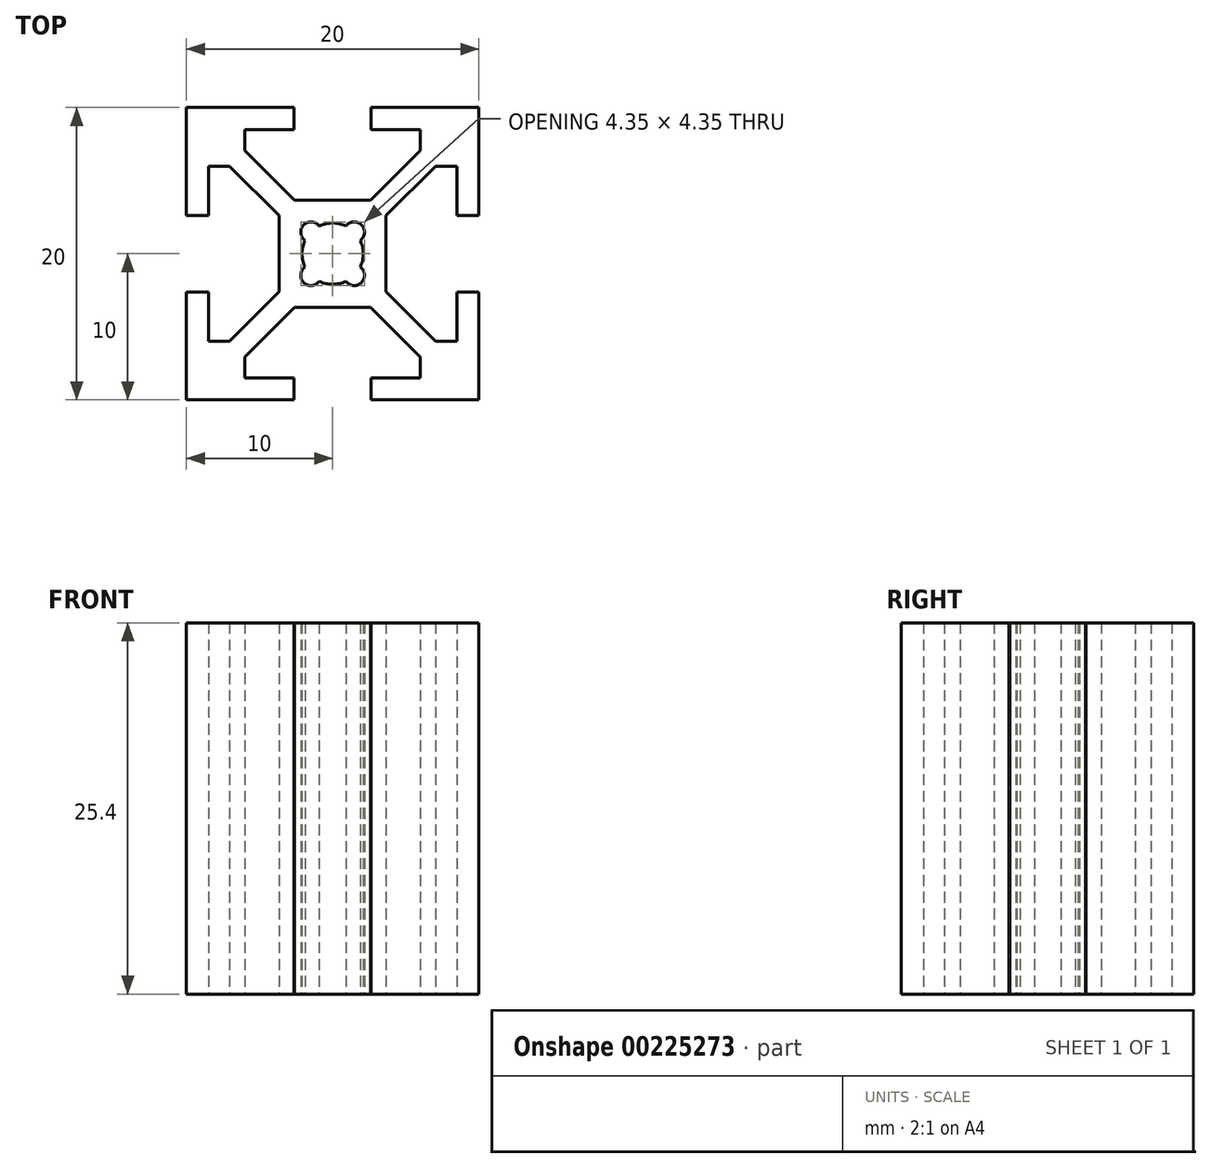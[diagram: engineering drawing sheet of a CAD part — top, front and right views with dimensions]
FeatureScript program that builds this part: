
annotation { "Feature Type Name" : "Feature", "Feature Type Description" : "" }
export const myFeature = defineFeature(function(context is Context, id is Id, definition is map)
    precondition{}
    {
        {
            var Q0;
            Q0=qCreatedBy(makeId("Top.planeOp"),FACE);
            var sketch = newSketch(context, id + "F0", { "sketchPlane" : qUnion([Q0])});
            skLineSegment(sketch, "E0.bottom", {"start": v(10, 10) * mm, "end": v(-10, 10) * mm});
            skLineSegment(sketch, "E0.top", {"start": v(10, -10) * mm, "end": v(-10, -10) * mm});
            skLineSegment(sketch, "E0.left", {"start": v(10, 10) * mm, "end": v(10, -10) * mm});
            skLineSegment(sketch, "E0.right", {"start": v(-10, 10) * mm, "end": v(-10, -10) * mm});
            skPoint(sketch, "E0.middle", {"position": v(0, 0) * mm});
            skLineSegment(sketch, "E1", {"start": v(-10, 10) * mm, "end": v(10, -10) * mm, "construction": true});
            skLineSegment(sketch, "E2", {"start": v(-10, -10) * mm, "end": v(10, 10) * mm, "construction": true});
            skLineSegment(sketch, "E3", {"start": v(0, 10) * mm, "end": v(0, -10) * mm, "construction": true});
            skLineSegment(sketch, "E4", {"start": v(-10, 0) * mm, "end": v(10, 0) * mm, "construction": true});
            skPoint(sketch, "E4.endSnap0", {"position": v(10, 0) * mm});
            skLineSegment(sketch, "E5", {"start": v(-2.63, 13.49) * mm, "end": v(2.63, 13.49) * mm});
            skLineSegment(sketch, "E6", {"start": v(2.63, 13.49) * mm, "end": v(2.63, 8.5) * mm});
            skLineSegment(sketch, "E7", {"start": v(2.63, 8.5) * mm, "end": v(6, 8.5) * mm});
            skLineSegment(sketch, "E8", {"start": v(6, 8.5) * mm, "end": v(6, 7.06) * mm});
            skLineSegment(sketch, "E9", {"start": v(6, 7.06) * mm, "end": v(2.6, 3.66) * mm});
            skLineSegment(sketch, "E10", {"start": v(2.6, 3.66) * mm, "end": v(-2.6, 3.66) * mm});
            skLineSegment(sketch, "E11", {"start": v(-2.6, 3.66) * mm, "end": v(-6, 7.06) * mm});
            skLineSegment(sketch, "E12", {"start": v(-6, 7.06) * mm, "end": v(-6, 8.5) * mm});
            skLineSegment(sketch, "E13", {"start": v(-6, 8.5) * mm, "end": v(-2.63, 8.5) * mm});
            skLineSegment(sketch, "E14", {"start": v(-2.63, 8.5) * mm, "end": v(-2.63, 13.49) * mm});
            skCircle(sketch, "E15", {"center": v(0, 0) * mm, "radius": 2.1 * mm});
            skLineSegment(sketch, "E16.MirrorCS", {"start": v(-7.06, 6) * mm, "end": v(-8.5, 6) * mm});
            skLineSegment(sketch, "E17.MirrorCS", {"start": v(-3.66, 2.6) * mm, "end": v(-7.06, 6) * mm});
            skLineSegment(sketch, "E18.MirrorCS", {"start": v(-8.5, 6) * mm, "end": v(-8.5, 2.63) * mm});
            skLineSegment(sketch, "E19.MirrorCS", {"start": v(-3.66, -2.6) * mm, "end": v(-3.66, 2.6) * mm});
            skLineSegment(sketch, "E20.MirrorCS", {"start": v(-7.06, -6) * mm, "end": v(-3.66, -2.6) * mm});
            skLineSegment(sketch, "E21.MirrorCS", {"start": v(-8.5, -6) * mm, "end": v(-7.06, -6) * mm});
            skLineSegment(sketch, "E22.MirrorCS", {"start": v(-8.5, -2.63) * mm, "end": v(-8.5, -6) * mm});
            skLineSegment(sketch, "E23.MirrorCS", {"start": v(-13.49, -2.63) * mm, "end": v(-8.5, -2.63) * mm});
            skLineSegment(sketch, "E24.MirrorCS", {"start": v(-13.49, 2.63) * mm, "end": v(-13.49, -2.63) * mm});
            skLineSegment(sketch, "E25.MirrorCS", {"start": v(-8.5, 2.63) * mm, "end": v(-13.49, 2.63) * mm});
            skLineSegment(sketch, "E26.MirrorCS", {"start": v(-2.6, -3.66) * mm, "end": v(-6, -7.06) * mm});
            skLineSegment(sketch, "E27.MirrorCS", {"start": v(2.6, -3.66) * mm, "end": v(-2.6, -3.66) * mm});
            skLineSegment(sketch, "E28.MirrorCS", {"start": v(6, -7.06) * mm, "end": v(2.6, -3.66) * mm});
            skLineSegment(sketch, "E29.MirrorCS", {"start": v(6, -8.5) * mm, "end": v(6, -7.06) * mm});
            skLineSegment(sketch, "E30.MirrorCS", {"start": v(2.63, -8.5) * mm, "end": v(6, -8.5) * mm});
            skLineSegment(sketch, "E31.MirrorCS", {"start": v(2.63, -13.49) * mm, "end": v(2.63, -8.5) * mm});
            skLineSegment(sketch, "E32.MirrorCS", {"start": v(-2.63, -13.49) * mm, "end": v(2.63, -13.49) * mm});
            skLineSegment(sketch, "E33.MirrorCS", {"start": v(-2.63, -8.5) * mm, "end": v(-2.63, -13.49) * mm});
            skLineSegment(sketch, "E34.MirrorCS", {"start": v(-6, -8.5) * mm, "end": v(-2.63, -8.5) * mm});
            skLineSegment(sketch, "E35.MirrorCS", {"start": v(-6, -7.06) * mm, "end": v(-6, -8.5) * mm});
            skLineSegment(sketch, "E36.MirrorCS", {"start": v(7.06, 6) * mm, "end": v(3.66, 2.6) * mm});
            skLineSegment(sketch, "E37.MirrorCS", {"start": v(8.5, 6) * mm, "end": v(7.06, 6) * mm});
            skLineSegment(sketch, "E38.MirrorCS", {"start": v(8.5, 2.63) * mm, "end": v(8.5, 6) * mm});
            skLineSegment(sketch, "E39.MirrorCS", {"start": v(13.49, 2.63) * mm, "end": v(8.5, 2.63) * mm});
            skLineSegment(sketch, "E40.MirrorCS", {"start": v(13.49, -2.63) * mm, "end": v(13.49, 2.63) * mm});
            skLineSegment(sketch, "E41.MirrorCS", {"start": v(8.5, -2.63) * mm, "end": v(13.49, -2.63) * mm});
            skLineSegment(sketch, "E42.MirrorCS", {"start": v(8.5, -6) * mm, "end": v(8.5, -2.63) * mm});
            skLineSegment(sketch, "E43.MirrorCS", {"start": v(7.06, -6) * mm, "end": v(8.5, -6) * mm});
            skLineSegment(sketch, "E44.MirrorCS", {"start": v(3.66, -2.6) * mm, "end": v(7.06, -6) * mm});
            skLineSegment(sketch, "E45.MirrorCS", {"start": v(3.66, 2.6) * mm, "end": v(3.66, -2.6) * mm});
            skCircle(sketch, "E46", {"center": v(-1.48, 1.48) * mm, "radius": 0.7 * mm});
            skCircle(sketch, "E47.MirrorC", {"center": v(1.48, 1.48) * mm, "radius": 0.7 * mm});
            skCircle(sketch, "E48.MirrorC", {"center": v(-1.48, -1.48) * mm, "radius": 0.7 * mm});
            skCircle(sketch, "E49.MirrorC", {"center": v(1.48, -1.48) * mm, "radius": 0.7 * mm});
            skSolve(sketch);
        }
        {
            var Q0;
            {var subQ29=sQuery(id+"F0.wireOp",EDGE,"E7");Q0=makeQuery(id+"F0.imprint","IMPRINT",FACE,{"disambiguationData":[TD([[makeQuery(id+"F0.imprint","IMPRINT",EDGE,{"derivedFrom":subQ29}),1.0]])]});}
            extrude(context, id + "F1", {"entities" : qUnion([Q0]), "depth" : 25.4 * mm});
        }
    });
